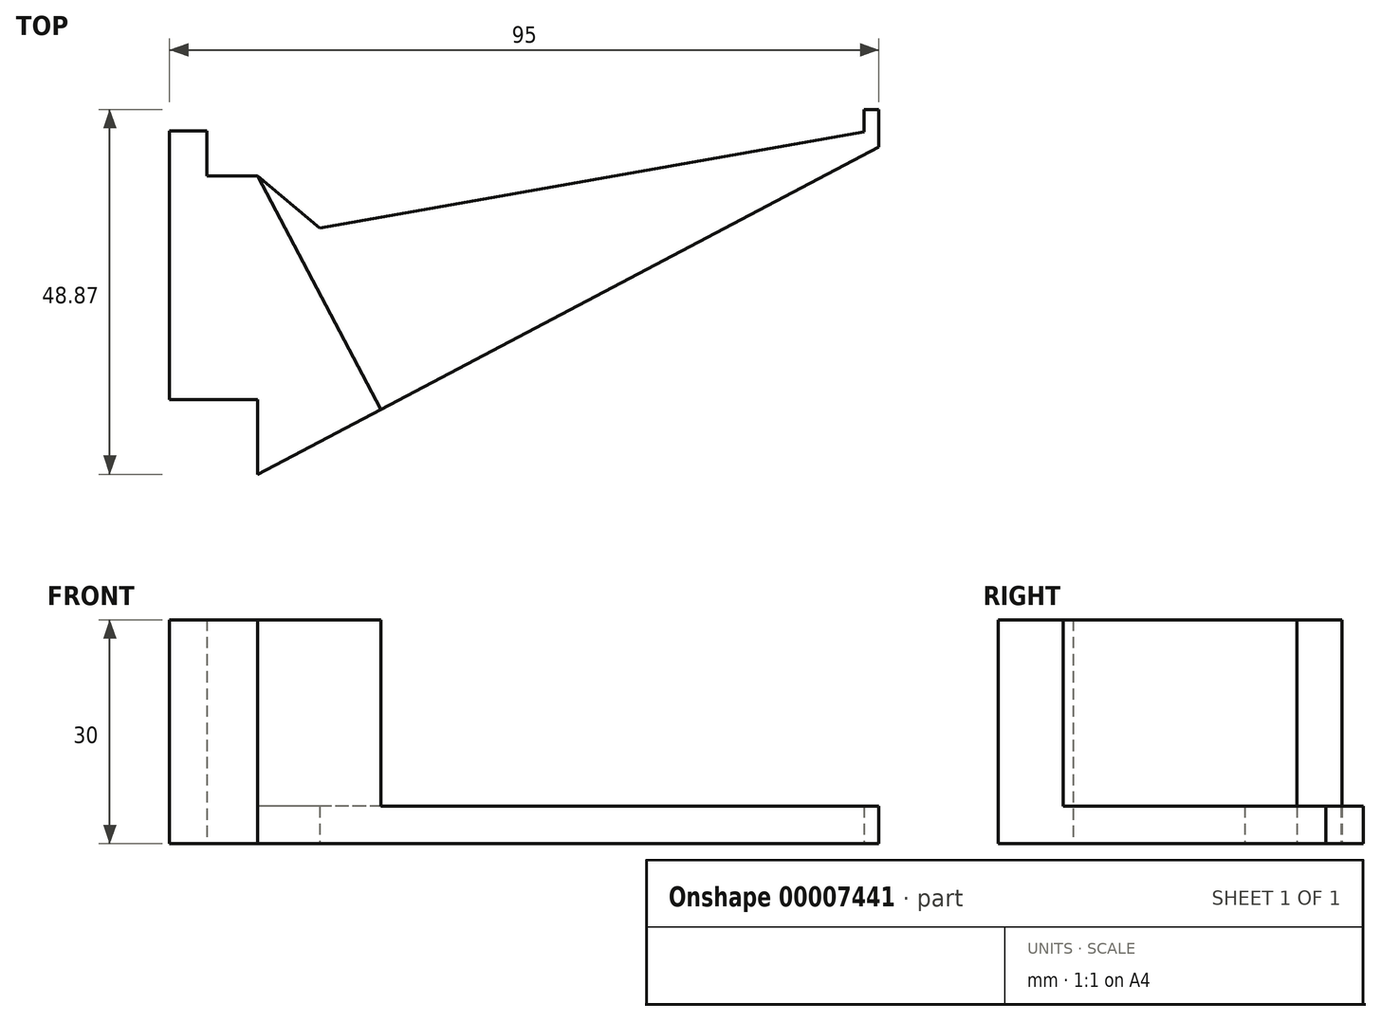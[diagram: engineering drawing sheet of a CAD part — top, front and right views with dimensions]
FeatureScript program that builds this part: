
annotation { "Feature Type Name" : "Feature", "Feature Type Description" : "" }
export const myFeature = defineFeature(function(context is Context, id is Id, definition is map)
    precondition{}
    {
        {
            var Q0;
            Q0=qCreatedBy(makeId("Top.planeOp"),FACE);
            var sketch = newSketch(context, id + "F0", { "sketchPlane" : qUnion([Q0])});
            skLineSegment(sketch, "E0", {"start": v(0, 0) * mm, "end": v(0, 36) * mm});
            skLineSegment(sketch, "E1", {"start": v(0, 36) * mm, "end": v(5, 36) * mm});
            skLineSegment(sketch, "E2", {"start": v(5, 36) * mm, "end": v(5, 30) * mm});
            skLineSegment(sketch, "E3", {"start": v(5, 30) * mm, "end": v(11.8, 30) * mm});
            skLineSegment(sketch, "E4", {"start": v(0, 0) * mm, "end": v(5, 0) * mm});
            skLineSegment(sketch, "E5", {"start": v(5, 0) * mm, "end": v(11.8, 0) * mm});
            skLineSegment(sketch, "E6", {"start": v(11.8, 0) * mm, "end": v(11.8, -10) * mm});
            skLineSegment(sketch, "E7", {"start": v(11.8, -10) * mm, "end": v(95, 33.87) * mm});
            skLineSegment(sketch, "E8", {"start": v(95, 33.87) * mm, "end": v(95, 38.87) * mm});
            skLineSegment(sketch, "E9", {"start": v(93, 38.87) * mm, "end": v(95, 38.87) * mm});
            skLineSegment(sketch, "E10", {"start": v(93, 38.87) * mm, "end": v(93, 35.87) * mm});
            skLineSegment(sketch, "E11", {"start": v(93, 35.87) * mm, "end": v(20.12, 23.02) * mm});
            skLineSegment(sketch, "E12", {"start": v(20.12, 23.02) * mm, "end": v(11.8, 30) * mm});
            skLineSegment(sketch, "E13", {"start": v(11.8, 30) * mm, "end": v(28.3, -1.3) * mm});
            skSolve(sketch);
        }
        {
            var Q0;
            Q0 = qSketchRegion(id + "F0", true);
            extrude(context, id + "F1", {"entities" : qUnion([Q0]), "depth" : 5 * mm});
        }
        {
            var Q0;
            Q0=makeQuery(id+"F0.imprint","IMPRINT",FACE,{"disambiguationData":[TD([[makeQuery(id+"F0.imprint","IMPRINT",EDGE,{"derivedFrom":sQuery(id+"F0.wireOp",EDGE,"E0")}),-1.0]])]});
            extrude(context, id + "F2", {"entities" : qUnion([Q0]), "operationType" : NewBodyOperationType.ADD, "depth" : 30 * mm});
        }
    });
